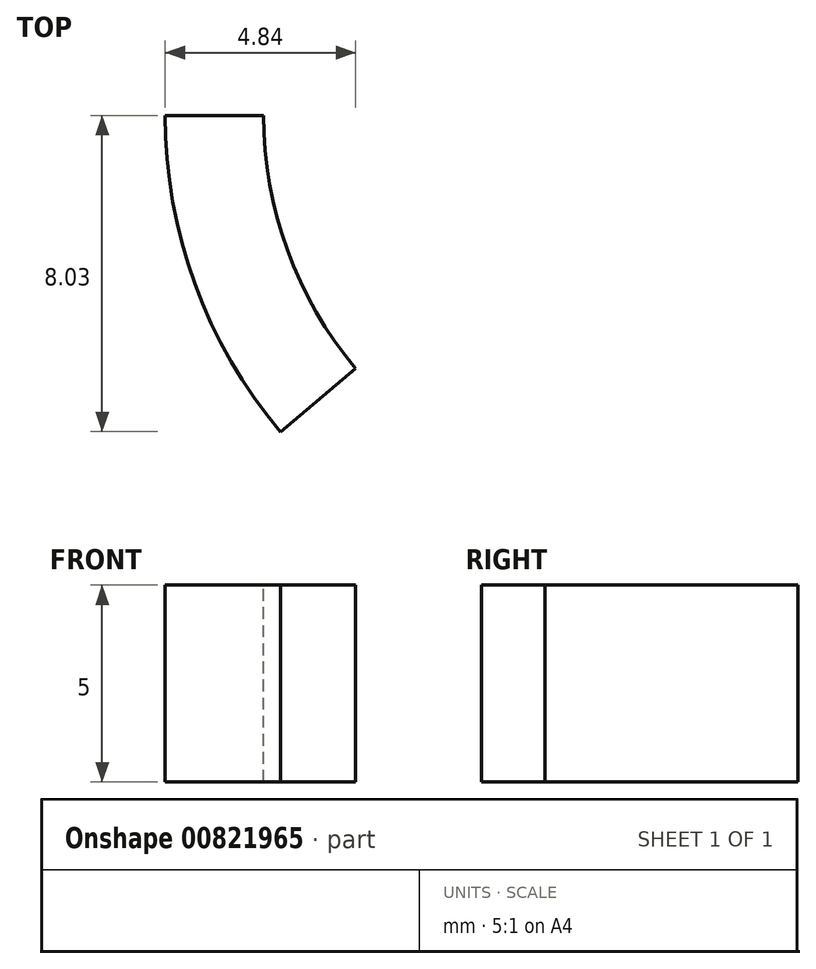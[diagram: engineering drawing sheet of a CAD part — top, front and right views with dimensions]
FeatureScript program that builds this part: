
annotation { "Feature Type Name" : "Feature", "Feature Type Description" : "" }
export const myFeature = defineFeature(function(context is Context, id is Id, definition is map)
    precondition{}
    {
        {
            var Q0;
            Q0=qCreatedBy(makeId("Front.planeOp"),FACE);
            var sketch = newSketch(context, id + "F0", { "sketchPlane" : qUnion([Q0])});
            skLineSegment(sketch, "E0.bottom", {"start": v(0, 0) * mm, "end": v(-2.5, 0) * mm});
            skLineSegment(sketch, "E0.top", {"start": v(0, 5) * mm, "end": v(-2.5, 5) * mm});
            skLineSegment(sketch, "E0.left", {"start": v(0, 0) * mm, "end": v(0, 5) * mm});
            skLineSegment(sketch, "E0.right", {"start": v(-2.5, 0) * mm, "end": v(-2.5, 5) * mm});
            skLineSegment(sketch, "E1", {"start": v(0, 0) * mm, "end": v(10, 0) * mm});
            skLineSegment(sketch, "E2", {"start": v(10, 0) * mm, "end": v(10, 21.04) * mm});
            skSolve(sketch);
        }
        {
            var Q0;
            Q0=qSketchRegion(id+"F0",true);
            var Q1;
            Q1=sQuery(id+"F0.wireOp",EDGE,"E2");
            revolve(context, id + "F1", {"surfaceOperationType" : NewSurfaceOperationType.NEW, "entities" : qUnion([Q0]), "axis" : qUnion([Q1]), "revolveType" : RevolveType.ONE_DIRECTION, "angle" : 40 * degree});
        }
    });
